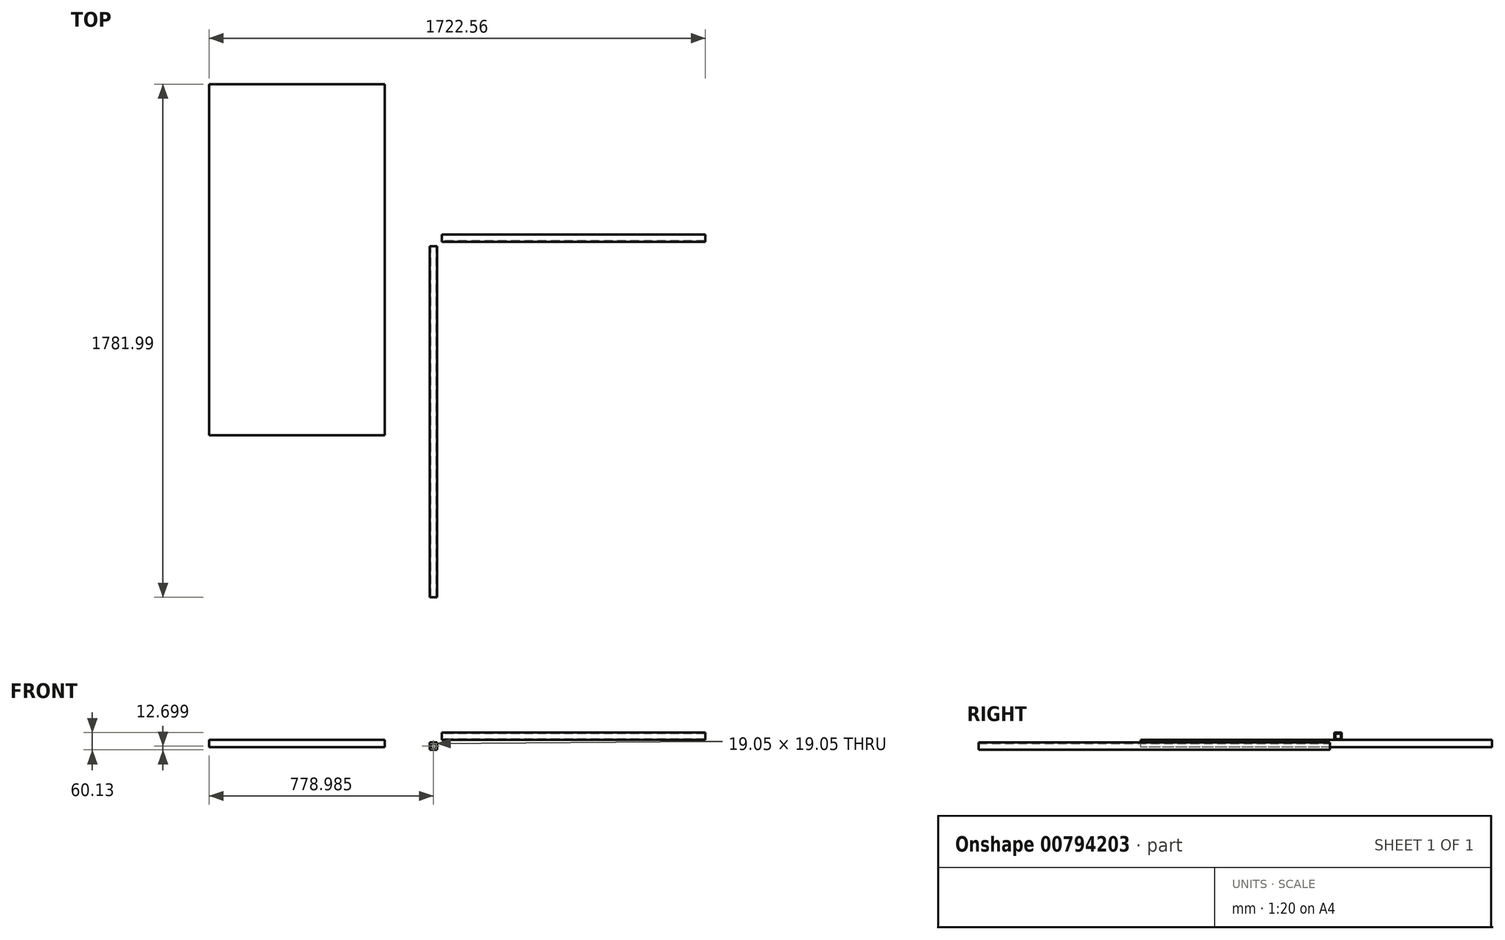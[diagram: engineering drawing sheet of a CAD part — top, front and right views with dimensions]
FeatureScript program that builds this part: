
annotation { "Feature Type Name" : "Feature", "Feature Type Description" : "" }
export const myFeature = defineFeature(function(context is Context, id is Id, definition is map)
    precondition{}
    {
        {
            var Q0;
            Q0=qCreatedBy(makeId("Right.planeOp"),FACE);
            var sketch = newSketch(context, id + "F0", { "sketchPlane" : qUnion([Q0])});
            skLineSegment(sketch, "E0.bottom", {"start": v(-130, -12.53) * mm, "end": v(-28.4, -12.53) * mm});
            skLineSegment(sketch, "E0.top", {"start": v(-130, -31.58) * mm, "end": v(-28.4, -31.58) * mm});
            skLineSegment(sketch, "E0.left", {"start": v(-130, -12.53) * mm, "end": v(-130, -31.58) * mm});
            skLineSegment(sketch, "E0.right", {"start": v(-28.4, -12.53) * mm, "end": v(-28.4, -31.58) * mm});
            skSolve(sketch);
        }
        {
            var Q0;
            Q0=qCreatedBy(makeId("Front.planeOp"),FACE);
            var sketch = newSketch(context, id + "F1", { "sketchPlane" : qUnion([Q0])});
            skLineSegment(sketch, "E1.bottom", {"start": v(44.51, 41.1) * mm, "end": v(146.11, 41.1) * mm});
            skLineSegment(sketch, "E1.top", {"start": v(44.51, 22.05) * mm, "end": v(146.11, 22.05) * mm});
            skLineSegment(sketch, "E1.left", {"start": v(44.51, 41.1) * mm, "end": v(44.51, 22.05) * mm});
            skLineSegment(sketch, "E1.right", {"start": v(146.11, 41.1) * mm, "end": v(146.11, 22.05) * mm});
            skSolve(sketch);
        }
        {
            var Q0;
            Q0=makeQuery(id+"F0.imprint","IMPRINT",FACE,{"disambiguationData":[TD([[makeQuery(id+"F0.imprint","IMPRINT",EDGE,{"derivedFrom":sQuery(id+"F0.wireOp",EDGE,"E0.bottom")}),-1.0]])]});
            extrude(context, id + "F2", {"entities" : qUnion([Q0]), "oppositeDirection" : true, "depth" : 609.6 * mm, "offsetDistance" : 25.4 * mm});
        }
        {
            var Q0;
            Q0=makeQuery(id+"F1.imprint","IMPRINT",FACE,{"disambiguationData":[TD([[makeQuery(id+"F1.imprint","IMPRINT",EDGE,{"derivedFrom":sQuery(id+"F1.wireOp",EDGE,"E1.bottom")}),-1.0]])]});
            extrude(context, id + "F3", {"entities" : qUnion([Q0]), "oppositeDirection" : true, "depth" : 1219.2 * mm, "offsetDistance" : 25.4 * mm});
        }
        {
            var Q0;
            Q0=makeQuery(id+"F3.opExtrude","SWEPT_BODY",BODY,{"disambiguationData":[OSD([sQuery(id+"F1.wireOp",EDGE,"E1.bottom"),sQuery(id+"F1.wireOp",EDGE,"E1.top"),sQuery(id+"F1.wireOp",EDGE,"E1.left"),sQuery(id+"F1.wireOp",EDGE,"E1.right")])]});
            var Q1;
            Q1=makeQuery(id+"F2.opExtrude","SWEPT_BODY",BODY,{"disambiguationData":[OSD([sQuery(id+"F0.wireOp",EDGE,"E0.bottom"),sQuery(id+"F0.wireOp",EDGE,"E0.top"),sQuery(id+"F0.wireOp",EDGE,"E0.left"),sQuery(id+"F0.wireOp",EDGE,"E0.right")])]});
            deleteBodies(context, id + "F4", {"entities" : qUnion([Q0, Q1])});
        }
        {
            var Q0;
            Q0=qCreatedBy(makeId("Top.planeOp"),FACE);
            var sketch = newSketch(context, id + "F5", { "sketchPlane" : qUnion([Q0])});
            skLineSegment(sketch, "E2.bottom", {"start": v(-808.16, 562.79) * mm, "end": v(-198.56, 562.79) * mm});
            skLineSegment(sketch, "E2.top", {"start": v(-808.16, -656.41) * mm, "end": v(-198.56, -656.41) * mm});
            skLineSegment(sketch, "E2.left", {"start": v(-808.16, 562.79) * mm, "end": v(-808.16, -656.41) * mm});
            skLineSegment(sketch, "E2.right", {"start": v(-198.56, 562.79) * mm, "end": v(-198.56, -656.41) * mm});
            skSolve(sketch);
        }
        {
            var Q0;
            Q0=makeQuery(id+"F5.imprint","IMPRINT",FACE,{"disambiguationData":[TD([[makeQuery(id+"F5.imprint","IMPRINT",EDGE,{"derivedFrom":sQuery(id+"F5.wireOp",EDGE,"E2.bottom")}),-1.0]])]});
            extrude(context, id + "F6", {"entities" : qUnion([Q0]), "oppositeDirection" : true, "depth" : 25.4 * mm, "offsetDistance" : 25.4 * mm});
        }
        {
            var Q0;
            Q0=qCreatedBy(makeId("Front.planeOp"),FACE);
            var sketch = newSketch(context, id + "F7", { "sketchPlane" : qUnion([Q0])});
            skLineSegment(sketch, "E3.bottom", {"start": v(-41.87, -9.33) * mm, "end": v(-16.47, -9.33) * mm});
            skLineSegment(sketch, "E3.top", {"start": v(-41.87, -34.73) * mm, "end": v(-16.47, -34.73) * mm});
            skLineSegment(sketch, "E3.left", {"start": v(-41.87, -9.33) * mm, "end": v(-41.87, -34.73) * mm});
            skLineSegment(sketch, "E3.right", {"start": v(-16.47, -9.33) * mm, "end": v(-16.47, -34.73) * mm});
            skLineSegment(sketch, "E4.0", {"start": v(-38.7, -12.5) * mm, "end": v(-19.65, -12.5) * mm});
            skLineSegment(sketch, "E4.1", {"start": v(-38.7, -12.5) * mm, "end": v(-38.7, -31.56) * mm});
            skLineSegment(sketch, "E4.2", {"start": v(-38.7, -31.56) * mm, "end": v(-19.65, -31.56) * mm});
            skLineSegment(sketch, "E4.3", {"start": v(-19.65, -12.5) * mm, "end": v(-19.65, -31.56) * mm});
            skSolve(sketch);
        }
        {
            var Q0;
            Q0=makeQuery(id+"F7.imprint","IMPRINT",FACE,{"disambiguationData":[TD([[makeQuery(id+"F7.imprint","IMPRINT",EDGE,{"derivedFrom":sQuery(id+"F7.wireOp",EDGE,"E3.bottom")}),-1.0]])]});
            extrude(context, id + "F8", {"entities" : qUnion([Q0]), "depth" : 1219.2 * mm, "offsetDistance" : 25.4 * mm});
        }
        {
            var Q0;
            Q0=qCreatedBy(makeId("Right.planeOp"),FACE);
            var sketch = newSketch(context, id + "F9", { "sketchPlane" : qUnion([Q0])});
            skLineSegment(sketch, "E5.bottom", {"start": v(15.55, 25.4) * mm, "end": v(40.95, 25.4) * mm});
            skLineSegment(sketch, "E5.top", {"start": v(15.55, 0) * mm, "end": v(40.95, 0) * mm});
            skLineSegment(sketch, "E5.left", {"start": v(15.55, 25.4) * mm, "end": v(15.55, 0) * mm});
            skLineSegment(sketch, "E5.right", {"start": v(40.95, 25.4) * mm, "end": v(40.95, 0) * mm});
            skLineSegment(sketch, "E6.0", {"start": v(18.73, 22.23) * mm, "end": v(37.78, 22.23) * mm});
            skLineSegment(sketch, "E6.1", {"start": v(18.73, 22.23) * mm, "end": v(18.73, 3.17) * mm});
            skLineSegment(sketch, "E6.2", {"start": v(18.73, 3.17) * mm, "end": v(37.78, 3.17) * mm});
            skLineSegment(sketch, "E6.3", {"start": v(37.78, 22.23) * mm, "end": v(37.78, 3.17) * mm});
            skSolve(sketch);
        }
        {
            var Q0;
            Q0=makeQuery(id+"F9.imprint","IMPRINT",FACE,{"disambiguationData":[TD([[makeQuery(id+"F9.imprint","IMPRINT",EDGE,{"derivedFrom":sQuery(id+"F9.wireOp",EDGE,"E5.bottom")}),-1.0]])]});
            extrude(context, id + "F10", {"entities" : qUnion([Q0]), "depth" : 914.4 * mm, "offsetDistance" : 25.4 * mm});
        }
    });
